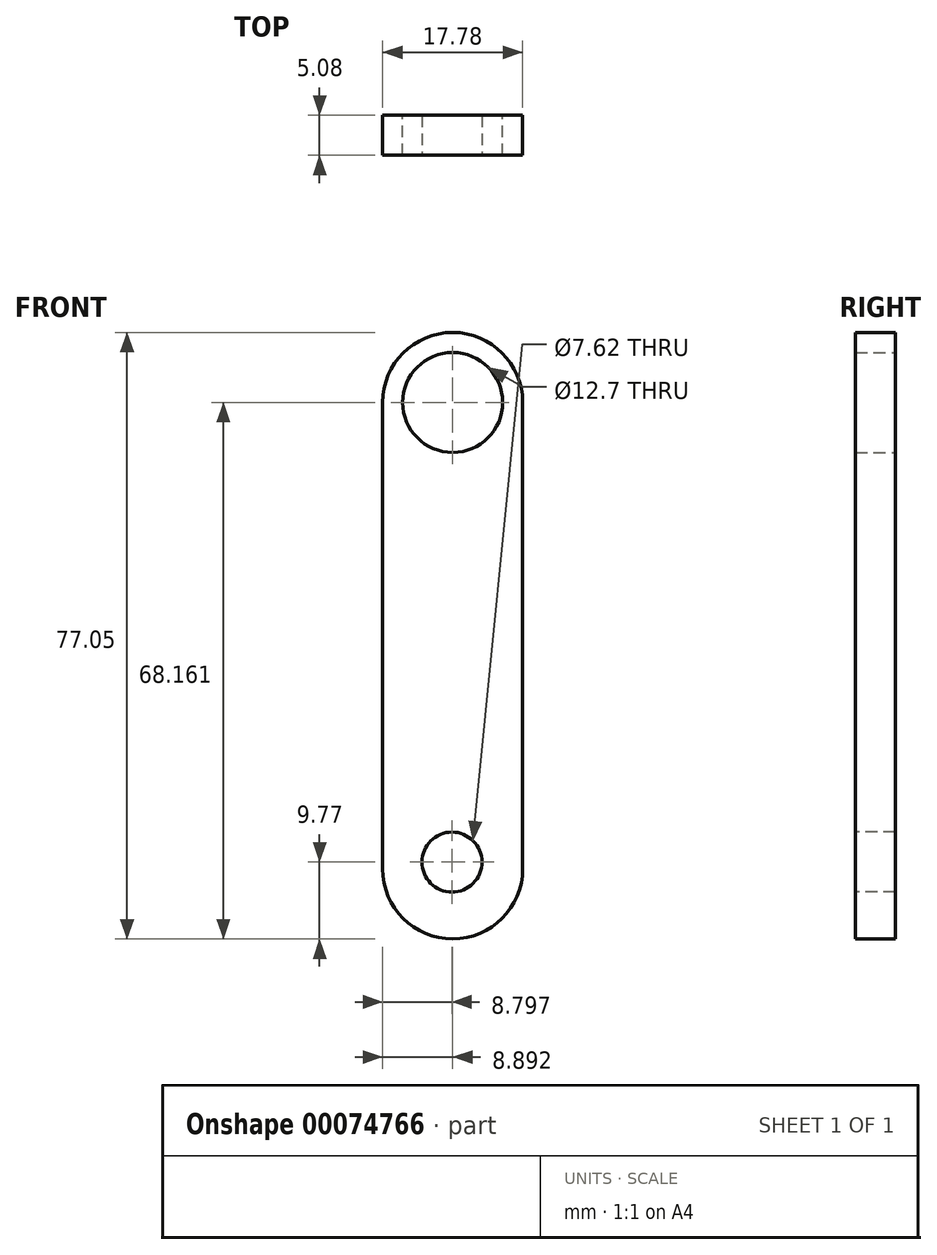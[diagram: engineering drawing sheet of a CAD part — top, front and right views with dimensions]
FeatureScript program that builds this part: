
annotation { "Feature Type Name" : "Feature", "Feature Type Description" : "" }
export const myFeature = defineFeature(function(context is Context, id is Id, definition is map)
    precondition{}
    {
        {
            var Q0;
            Q0=qCreatedBy(makeId("Front.planeOp"),FACE);
            var sketch = newSketch(context, id + "F0", { "sketchPlane" : qUnion([Q0])});
            skLineSegment(sketch, "E0", {"start": v(-58.72, 58.4) * mm, "end": v(-58.72, -0.88) * mm});
            skLineSegment(sketch, "E1", {"start": v(-40.94, 58.4) * mm, "end": v(-40.94, -0.88) * mm});
            skArc(sketch, "E2", {"start": v(-40.94, 58.4) * mm, "mid": v(-49.83, 67.28) * mm, "end": v(-58.72, 58.4) * mm});
            skArc(sketch, "E3", {"start": v(-58.72, -0.88) * mm, "mid": v(-49.83, -9.77) * mm, "end": v(-40.94, -0.88) * mm});
            skSolve(sketch);
        }
        {
            var Q0;
            Q0=makeQuery(id+"F0.imprint","IMPRINT",FACE,{"disambiguationData":[TD([[makeQuery(id+"F0.imprint","IMPRINT",EDGE,{"derivedFrom":sQuery(id+"F0.wireOp",EDGE,"E0")}),1.0]])]});
            extrude(context, id + "F1", {"entities" : qUnion([Q0]), "depth" : 5.08 * mm});
        }
        {
            var Q0;
            Q0=qCreatedBy(makeId("Front.planeOp"),FACE);
            var sketch = newSketch(context, id + "F2", { "sketchPlane" : qUnion([Q0])});
            skPoint(sketch, "E4", {"position": v(-49.92, 0) * mm});
            skSolve(sketch);
        }
        {
            var Q0;
            Q0=sQuery(id+"F2.wireOp",VERTEX,"E4");
            var Q1;
            Q1=makeQuery(id+"F1.opExtrude","SWEPT_BODY",BODY,{"disambiguationData":[OSD([sQuery(id+"F0.wireOp",EDGE,"E0"),sQuery(id+"F0.wireOp",EDGE,"E1"),sQuery(id+"F0.wireOp",EDGE,"E2"),sQuery(id+"F0.wireOp",EDGE,"E3")])]});
            hole(context, id + "F3", {"style" : HoleStyle.SIMPLE, "holeDiameter" : 7.62 * mm, "endStyle" : HoleEndStyle.THROUGH, "oppositeDirection" : true, "locations" : qUnion([Q0]), "scope" : qUnion([Q1])});
        }
        {
            var Q0;
            Q0=makeQuery(id+"F1.opExtrude","CAP_FACE",FACE,{"disambiguationData":[OSD([sQuery(id+"F0.wireOp",EDGE,"E0"),sQuery(id+"F0.wireOp",EDGE,"E1"),sQuery(id+"F0.wireOp",EDGE,"E2"),sQuery(id+"F0.wireOp",EDGE,"E3")])],"isStart":false});
            var sketch = newSketch(context, id + "F4", { "sketchPlane" : qUnion([Q0])});
            skPoint(sketch, "E5", {"position": v(-49.83, 58.4) * mm});
            skSolve(sketch);
        }
        {
            var Q0;
            Q0=sQuery(id+"F4.wireOp",VERTEX,"E5");
            var Q1;
            Q1=makeQuery(id+"F1.opExtrude","SWEPT_BODY",BODY,{"disambiguationData":[OSD([sQuery(id+"F0.wireOp",EDGE,"E0"),sQuery(id+"F0.wireOp",EDGE,"E1"),sQuery(id+"F0.wireOp",EDGE,"E2"),sQuery(id+"F0.wireOp",EDGE,"E3")])]});
            hole(context, id + "F5", {"style" : HoleStyle.SIMPLE, "holeDiameter" : 12.7 * mm, "endStyle" : HoleEndStyle.THROUGH, "locations" : qUnion([Q0]), "scope" : qUnion([Q1])});
        }
    });
